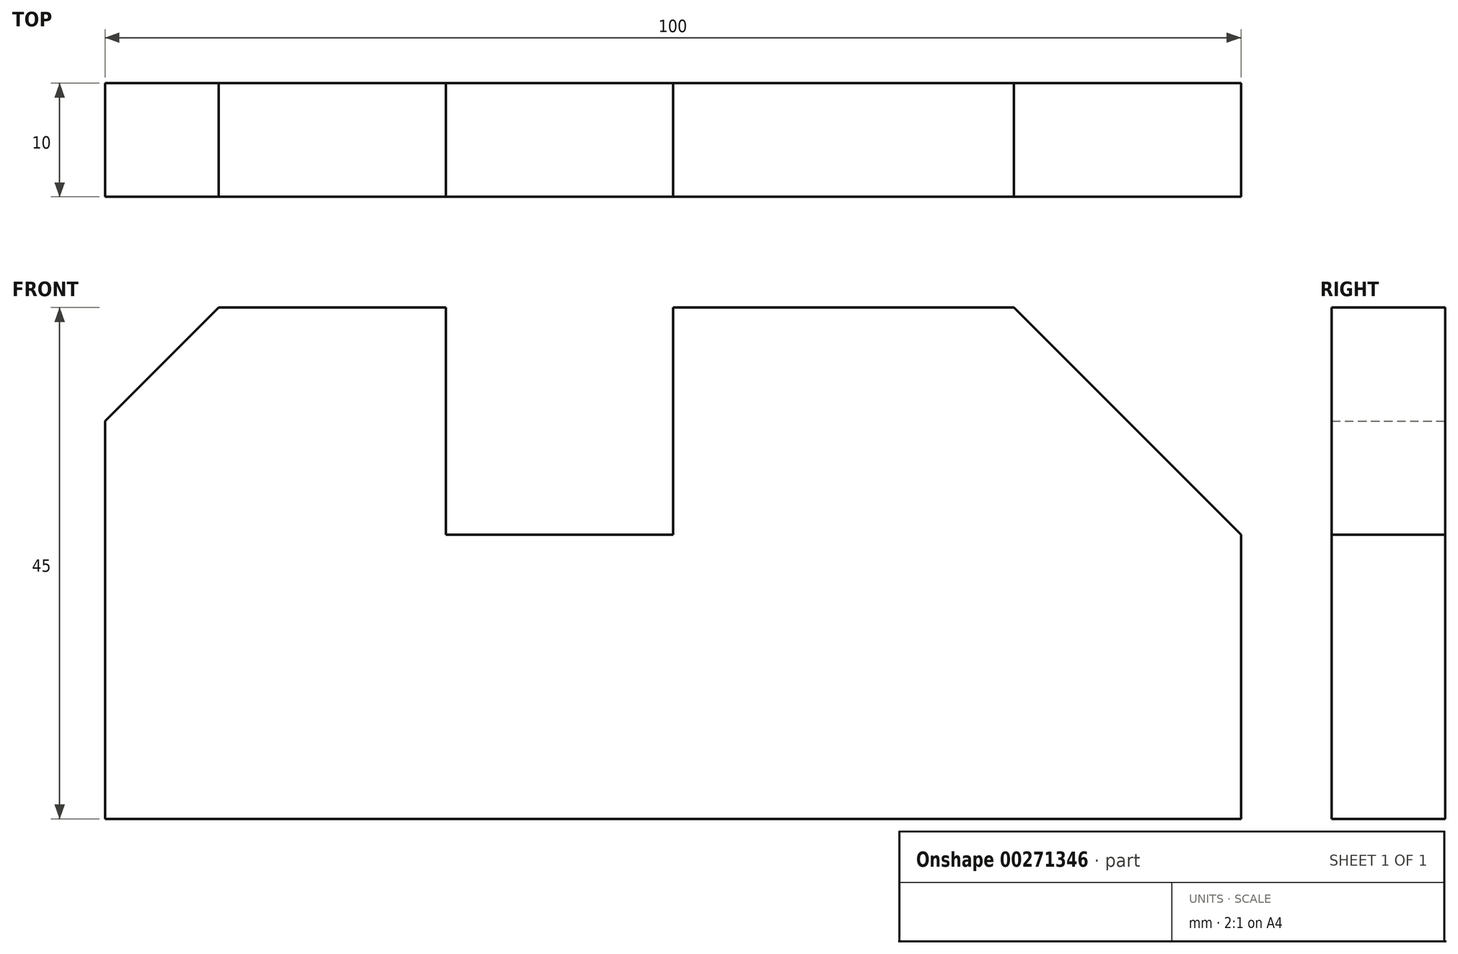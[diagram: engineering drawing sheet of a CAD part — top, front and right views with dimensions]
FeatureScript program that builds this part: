
annotation { "Feature Type Name" : "Feature", "Feature Type Description" : "" }
export const myFeature = defineFeature(function(context is Context, id is Id, definition is map)
    precondition{}
    {
        {
            var Q0;
            Q0=qCreatedBy(makeId("Front.planeOp"),FACE);
            var sketch = newSketch(context, id + "F0", { "sketchPlane" : qUnion([Q0])});
            skLineSegment(sketch, "E0", {"start": v(0, 0) * mm, "end": v(100, 0) * mm});
            skLineSegment(sketch, "E1", {"start": v(100, 0) * mm, "end": v(100, 25) * mm});
            skLineSegment(sketch, "E2", {"start": v(80, 45) * mm, "end": v(100, 25) * mm});
            skLineSegment(sketch, "E3", {"start": v(80, 45) * mm, "end": v(50, 45) * mm});
            skLineSegment(sketch, "E4", {"start": v(50, 45) * mm, "end": v(50, 25) * mm});
            skLineSegment(sketch, "E5", {"start": v(50, 25) * mm, "end": v(30, 25) * mm});
            skLineSegment(sketch, "E6", {"start": v(30, 25) * mm, "end": v(30, 45) * mm});
            skLineSegment(sketch, "E7", {"start": v(30, 45) * mm, "end": v(10, 45) * mm});
            skLineSegment(sketch, "E8", {"start": v(0, 35) * mm, "end": v(10, 45) * mm});
            skLineSegment(sketch, "E9", {"start": v(0, 35) * mm, "end": v(0, 0) * mm});
            skSolve(sketch);
        }
        {
            var Q0;
            Q0=makeQuery(id+"F0.imprint","IMPRINT",FACE,{"disambiguationData":[TD([[makeQuery(id+"F0.imprint","IMPRINT",EDGE,{"derivedFrom":sQuery(id+"F0.wireOp",EDGE,"E0")}),1.0]])]});
            extrude(context, id + "F1", {"entities" : qUnion([Q0]), "depth" : 10 * mm});
        }
    });
